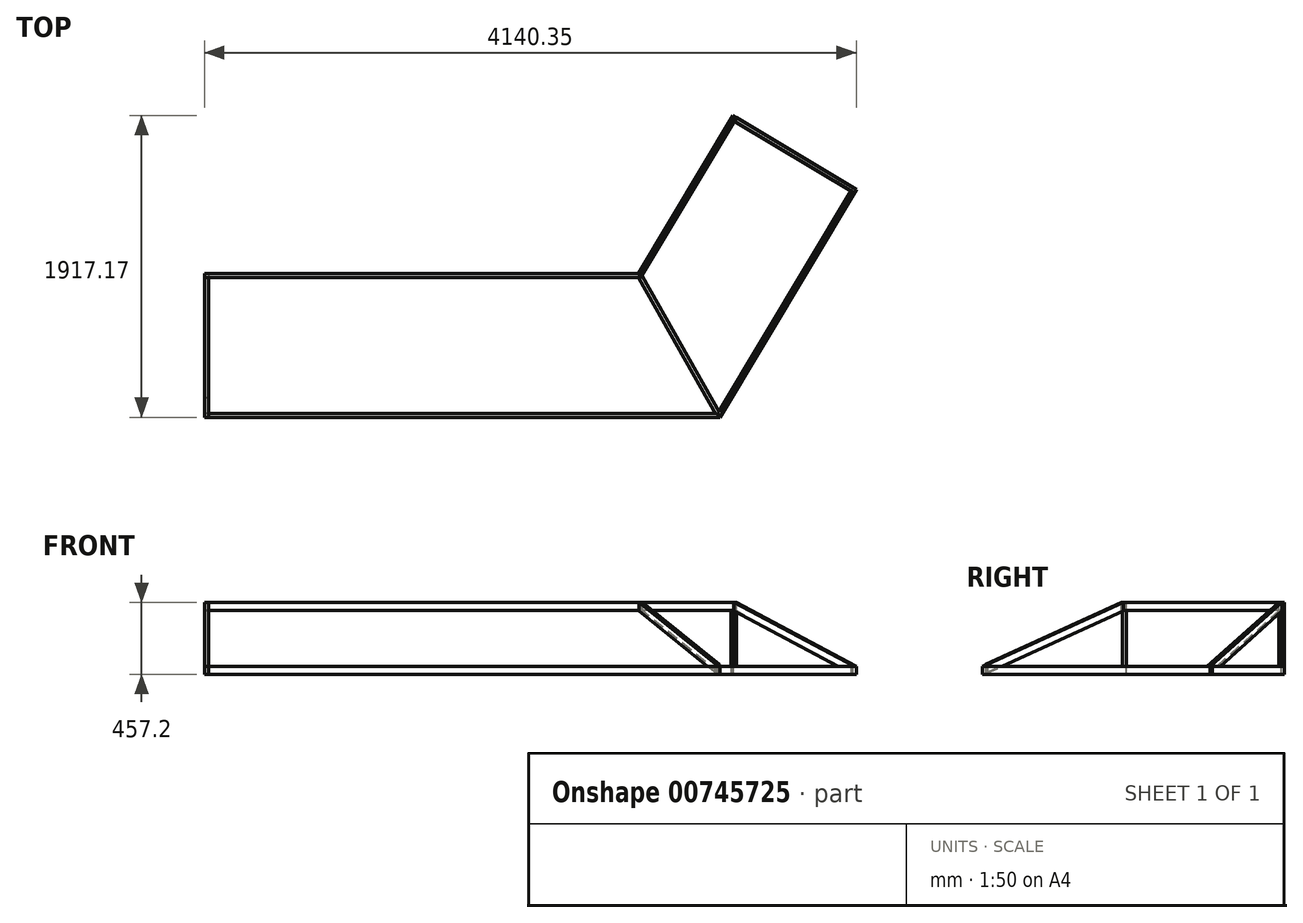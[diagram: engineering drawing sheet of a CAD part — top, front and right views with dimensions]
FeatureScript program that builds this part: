
annotation { "Feature Type Name" : "Feature", "Feature Type Description" : "" }
export const myFeature = defineFeature(function(context is Context, id is Id, definition is map)
    precondition{}
    {
        {
            var Q0;
            Q0=qCreatedBy(makeId("Top.planeOp"),FACE);
            var sketch = newSketch(context, id + "F0", { "sketchPlane" : qUnion([Q0])});
            skLineSegment(sketch, "E0", {"start": v(0, 0) * mm, "end": v(2755.9, 0) * mm});
            skLineSegment(sketch, "E1", {"start": v(2755.9, 0) * mm, "end": v(3355.57, 1002.77) * mm});
            skLineSegment(sketch, "E2", {"start": v(3355.57, 1002.77) * mm, "end": v(3377.37, 989.74) * mm});
            skLineSegment(sketch, "E3", {"start": v(3377.37, 989.74) * mm, "end": v(2770.3, -25.4) * mm});
            skLineSegment(sketch, "E4", {"start": v(2770.3, -25.4) * mm, "end": v(0, -25.4) * mm});
            skLineSegment(sketch, "E5", {"start": v(0, -25.4) * mm, "end": v(0, 0) * mm});
            skLineSegment(sketch, "E6", {"start": v(2755.9, 0) * mm, "end": v(2770.3, -25.4) * mm});
            skSolve(sketch);
        }
        {
            var Q0;
            Q0=makeQuery(id+"F0.imprint","IMPRINT",FACE,{"disambiguationData":[TD([[makeQuery(id+"F0.imprint","IMPRINT",EDGE,{"derivedFrom":sQuery(id+"F0.wireOp",EDGE,"E0")}),-1.0]])]});
            extrude(context, id + "F1", {"entities" : qUnion([Q0]), "oppositeDirection" : true, "depth" : 50.8 * mm, "offsetDistance" : 25.4 * mm});
        }
        {
            var Q0;
            Q0=makeQuery(id+"F0.imprint","IMPRINT",FACE,{"disambiguationData":[TD([[makeQuery(id+"F0.imprint","IMPRINT",EDGE,{"derivedFrom":sQuery(id+"F0.wireOp",EDGE,"E1")}),-1.0]])]});
            extrude(context, id + "F2", {"entities" : qUnion([Q0]), "oppositeDirection" : true, "depth" : 50.8 * mm, "offsetDistance" : 25.4 * mm});
        }
        {
            var Q0;
            Q0=qCreatedBy(makeId("Right.planeOp"),FACE);
            var sketch = newSketch(context, id + "F3", { "sketchPlane" : qUnion([Q0])});
            skLineSegment(sketch, "E7", {"start": v(-25.4, -55.86) * mm, "end": v(-25.4, 0) * mm});
            skLineSegment(sketch, "E8", {"start": v(-25.4, 0) * mm, "end": v(-914.4, -406.4) * mm});
            skLineSegment(sketch, "E9", {"start": v(-914.4, -406.4) * mm, "end": v(-792.21, -406.4) * mm});
            skLineSegment(sketch, "E10", {"start": v(-792.21, -406.4) * mm, "end": v(-25.4, -55.86) * mm});
            skLineSegment(sketch, "E11", {"start": v(-914.4, -406.4) * mm, "end": v(-914.4, -457.2) * mm});
            skLineSegment(sketch, "E12", {"start": v(-914.4, -457.2) * mm, "end": v(-889, -457.2) * mm});
            skLineSegment(sketch, "E13", {"start": v(-889, -457.2) * mm, "end": v(-889, -406.4) * mm});
            skLineSegment(sketch, "E14", {"start": v(-889, -457.2) * mm, "end": v(0, -457.2) * mm});
            skLineSegment(sketch, "E15", {"start": v(0, -457.2) * mm, "end": v(0, -406.4) * mm});
            skLineSegment(sketch, "E16", {"start": v(0, -406.4) * mm, "end": v(-889, -406.4) * mm});
            skLineSegment(sketch, "E17.bottom", {"start": v(0, -50.8) * mm, "end": v(-25.4, -50.8) * mm});
            skLineSegment(sketch, "E17.top", {"start": v(0, -406.4) * mm, "end": v(-25.4, -406.4) * mm});
            skLineSegment(sketch, "E17.left", {"start": v(0, -50.8) * mm, "end": v(0, -406.4) * mm});
            skLineSegment(sketch, "E17.right", {"start": v(-25.4, -50.8) * mm, "end": v(-25.4, -406.4) * mm});
            skSolve(sketch);
        }
        {
            var Q0;
            {var subQ2=sQuery(id+"F3.wireOp",EDGE,"E7");Q0=makeQuery(id+"F3.imprint","IMPRINT",FACE,{"disambiguationData":[TD([[makeQuery(id+"F3.imprint","IMPRINT",EDGE,{"derivedFrom":subQ2}),1.0]])]});}
            extrude(context, id + "F4", {"entities" : qUnion([Q0]), "depth" : 25.4 * mm, "offsetDistance" : 25.4 * mm});
        }
        {
            var Q0;
            {var subQ1=sQuery(id+"F3.wireOp",EDGE,"E17.bottom");Q0=makeQuery(id+"F3.imprint","IMPRINT",FACE,{"disambiguationData":[TD([[makeQuery(id+"F3.imprint","IMPRINT",EDGE,{"derivedFrom":subQ1}),1.0]])]});}
            extrude(context, id + "F5", {"entities" : qUnion([Q0]), "depth" : 25.4 * mm, "offsetDistance" : 25.4 * mm});
        }
        {
            var Q0;
            {var subQ3=sQuery(id+"F3.wireOp",EDGE,"E13");Q0=makeQuery(id+"F3.imprint","IMPRINT",FACE,{"disambiguationData":[TD([[makeQuery(id+"F3.imprint","IMPRINT",EDGE,{"derivedFrom":subQ3}),-1.0]])]});}
            extrude(context, id + "F6", {"entities" : qUnion([Q0]), "depth" : 25.4 * mm, "offsetDistance" : 25.4 * mm});
        }
        {
            var Q0;
            Q0=makeQuery(id+"F2.opExtrude","SWEPT_FACE",FACE,{"disambiguationData":[OSD([sQuery(id+"F0.wireOp",EDGE,"E2")])]});
            var sketch = newSketch(context, id + "F7", { "sketchPlane" : qUnion([Q0])});
            skLineSegment(sketch, "E18", {"start": v(-2390.63, 0) * mm, "end": v(-3279.63, -406.4) * mm});
            skLineSegment(sketch, "E19", {"start": v(-3279.63, -406.4) * mm, "end": v(-3157.45, -406.4) * mm});
            skLineSegment(sketch, "E20", {"start": v(-3157.45, -406.4) * mm, "end": v(-2390.63, -55.86) * mm});
            skLineSegment(sketch, "E21", {"start": v(-2390.63, -55.86) * mm, "end": v(-2390.63, 0) * mm});
            skLineSegment(sketch, "E22.bottom", {"start": v(-3279.63, -406.4) * mm, "end": v(-3254.23, -406.4) * mm});
            skLineSegment(sketch, "E22.top", {"start": v(-3279.63, -457.2) * mm, "end": v(-3254.23, -457.2) * mm});
            skLineSegment(sketch, "E22.left", {"start": v(-3279.63, -406.4) * mm, "end": v(-3279.63, -457.2) * mm});
            skLineSegment(sketch, "E22.right", {"start": v(-3254.23, -406.4) * mm, "end": v(-3254.23, -457.2) * mm});
            skLineSegment(sketch, "E23.bottom", {"start": v(-3254.23, -406.4) * mm, "end": v(-2365.23, -406.4) * mm});
            skLineSegment(sketch, "E23.top", {"start": v(-3254.23, -457.2) * mm, "end": v(-2365.23, -457.2) * mm});
            skLineSegment(sketch, "E23.right", {"start": v(-2365.23, -406.4) * mm, "end": v(-2365.23, -457.2) * mm});
            skLineSegment(sketch, "E24.bottom", {"start": v(-2365.23, -50.8) * mm, "end": v(-2390.63, -50.8) * mm});
            skLineSegment(sketch, "E24.top", {"start": v(-2365.23, -406.4) * mm, "end": v(-2390.63, -406.4) * mm});
            skLineSegment(sketch, "E24.left", {"start": v(-2365.23, -50.8) * mm, "end": v(-2365.23, -406.4) * mm});
            skLineSegment(sketch, "E24.right", {"start": v(-2390.63, -50.8) * mm, "end": v(-2390.63, -406.4) * mm});
            skSolve(sketch);
        }
        {
            var Q0;
            Q0=makeQuery(id+"F7.imprint","IMPRINT",FACE,{"disambiguationData":[TD([[makeQuery(id+"F7.imprint","IMPRINT",EDGE,{"derivedFrom":sQuery(id+"F7.wireOp",EDGE,"E18")}),1.0]])]});
            extrude(context, id + "F8", {"entities" : qUnion([Q0]), "oppositeDirection" : true, "depth" : 25.4 * mm, "offsetDistance" : 25.4 * mm});
        }
        {
            var Q0;
            {var subQ1=sQuery(id+"F7.wireOp",EDGE,"E24.bottom");Q0=makeQuery(id+"F7.imprint","IMPRINT",FACE,{"disambiguationData":[TD([[makeQuery(id+"F7.imprint","IMPRINT",EDGE,{"derivedFrom":subQ1}),1.0]])]});}
            extrude(context, id + "F9", {"entities" : qUnion([Q0]), "oppositeDirection" : true, "depth" : 25.4 * mm, "offsetDistance" : 25.4 * mm});
        }
        {
            var Q0;
            Q0=makeQuery(id+"F7.imprint","IMPRINT",FACE,{"disambiguationData":[TD([[makeQuery(id+"F7.imprint","IMPRINT",EDGE,{"derivedFrom":sQuery(id+"F7.wireOp",EDGE,"E23.top")}),1.0]])]});
            extrude(context, id + "F10", {"entities" : qUnion([Q0]), "oppositeDirection" : true, "depth" : 25.4 * mm, "offsetDistance" : 25.4 * mm});
        }
        {
            var Q0;
            Q0=makeQuery(id+"F4.opExtrude","SWEPT_FACE",FACE,{"disambiguationData":[OSD([sQuery(id+"F3.wireOp",EDGE,"E9"),sQuery(id+"F3.wireOp",EDGE,"E16")])]});
            var sketch = newSketch(context, id + "F11", { "sketchPlane" : qUnion([Q0])});
            skLineSegment(sketch, "E25", {"start": v(0, 914.4) * mm, "end": v(3274.5, 914.4) * mm});
            skLineSegment(sketch, "E26", {"start": v(3274.5, 914.4) * mm, "end": v(4140.35, -533.46) * mm});
            skLineSegment(sketch, "E27", {"start": v(4140.35, -533.46) * mm, "end": v(4118.55, -546.5) * mm});
            skLineSegment(sketch, "E28", {"start": v(4118.55, -546.5) * mm, "end": v(3260.1, 889) * mm});
            skLineSegment(sketch, "E29", {"start": v(3260.1, 889) * mm, "end": v(0, 889) * mm});
            skLineSegment(sketch, "E30", {"start": v(0, 889) * mm, "end": v(0, 914.4) * mm});
            skLineSegment(sketch, "E31", {"start": v(3260.1, 889) * mm, "end": v(3274.5, 914.4) * mm});
            skSolve(sketch);
        }
        {
            var Q0;
            {var subQ3=sQuery(id+"F11.wireOp",EDGE,"E31");Q0=makeQuery(id+"F11.imprint","IMPRINT",FACE,{"disambiguationData":[TD([[makeQuery(id+"F11.imprint","IMPRINT",EDGE,{"derivedFrom":subQ3}),1.0]])]});}
            extrude(context, id + "F12", {"entities" : qUnion([Q0]), "depth" : 50.8 * mm, "offsetDistance" : 25.4 * mm});
        }
        {
            var Q0;
            Q0=makeQuery(id+"F11.imprint","IMPRINT",FACE,{"disambiguationData":[TD([[makeQuery(id+"F11.imprint","IMPRINT",EDGE,{"derivedFrom":sQuery(id+"F11.wireOp",EDGE,"E26")}),-1.0]])]});
            extrude(context, id + "F13", {"entities" : qUnion([Q0]), "depth" : 50.8 * mm, "offsetDistance" : 25.4 * mm});
        }
        {
            var Q0;
            Q0=makeQuery(id+"F1.opExtrude","CAP_VERTEX",VERTEX,{"disambiguationData":[OSD([sQuery(id+"F0.wireOp",EDGE,"E3"),sQuery(id+"F0.wireOp",EDGE,"E4"),sQuery(id+"F0.wireOp",EDGE,"E6")])],"isStart":false});
            var Q1;
            Q1=makeQuery(id+"F1.opExtrude","CAP_VERTEX",VERTEX,{"disambiguationData":[OSD([sQuery(id+"F0.wireOp",EDGE,"E3"),sQuery(id+"F0.wireOp",EDGE,"E4"),sQuery(id+"F0.wireOp",EDGE,"E6")])],"isStart":true});
            var Q2;
            Q2=sQuery(id+"F11.wireOp",VERTEX,"E31.start");
            cPlane(context, id + "F14", {"entities" : qUnion([Q0, Q1, Q2]), "cplaneType" : CPlaneType.THREE_POINT, "offset" : 25.4 * mm, "width" : 152.4 * mm, "height" : 152.4 * mm});
        }
        {
            var Q0;
            Q0=qCreatedBy(id+"F14.planeOp",FACE);
            var sketch = newSketch(context, id + "F15", { "sketchPlane" : qUnion([Q0])});
            skLineSegment(sketch, "E32", {"start": v(1388.78, 0) * mm, "end": v(2381.6, -394.79) * mm});
            skLineSegment(sketch, "E33", {"start": v(2381.6, -394.79) * mm, "end": v(2381.6, -449.46) * mm});
            skLineSegment(sketch, "E34", {"start": v(2381.6, -449.46) * mm, "end": v(1388.78, -54.67) * mm});
            skLineSegment(sketch, "E35", {"start": v(1388.78, -54.67) * mm, "end": v(1388.78, 0) * mm});
            skSolve(sketch);
        }
        {
            var Q0;
            Q0 = qSketchRegion(id + "F15", true);
            extrude(context, id + "F16", {"entities" : qUnion([Q0]), "depth" : 12.7 * mm, "offsetDistance" : 25.4 * mm, "hasSecondDirection" : true, "secondDirectionOppositeDirection" : true, "secondDirectionDepth" : 12.7 * mm});
        }
    });
